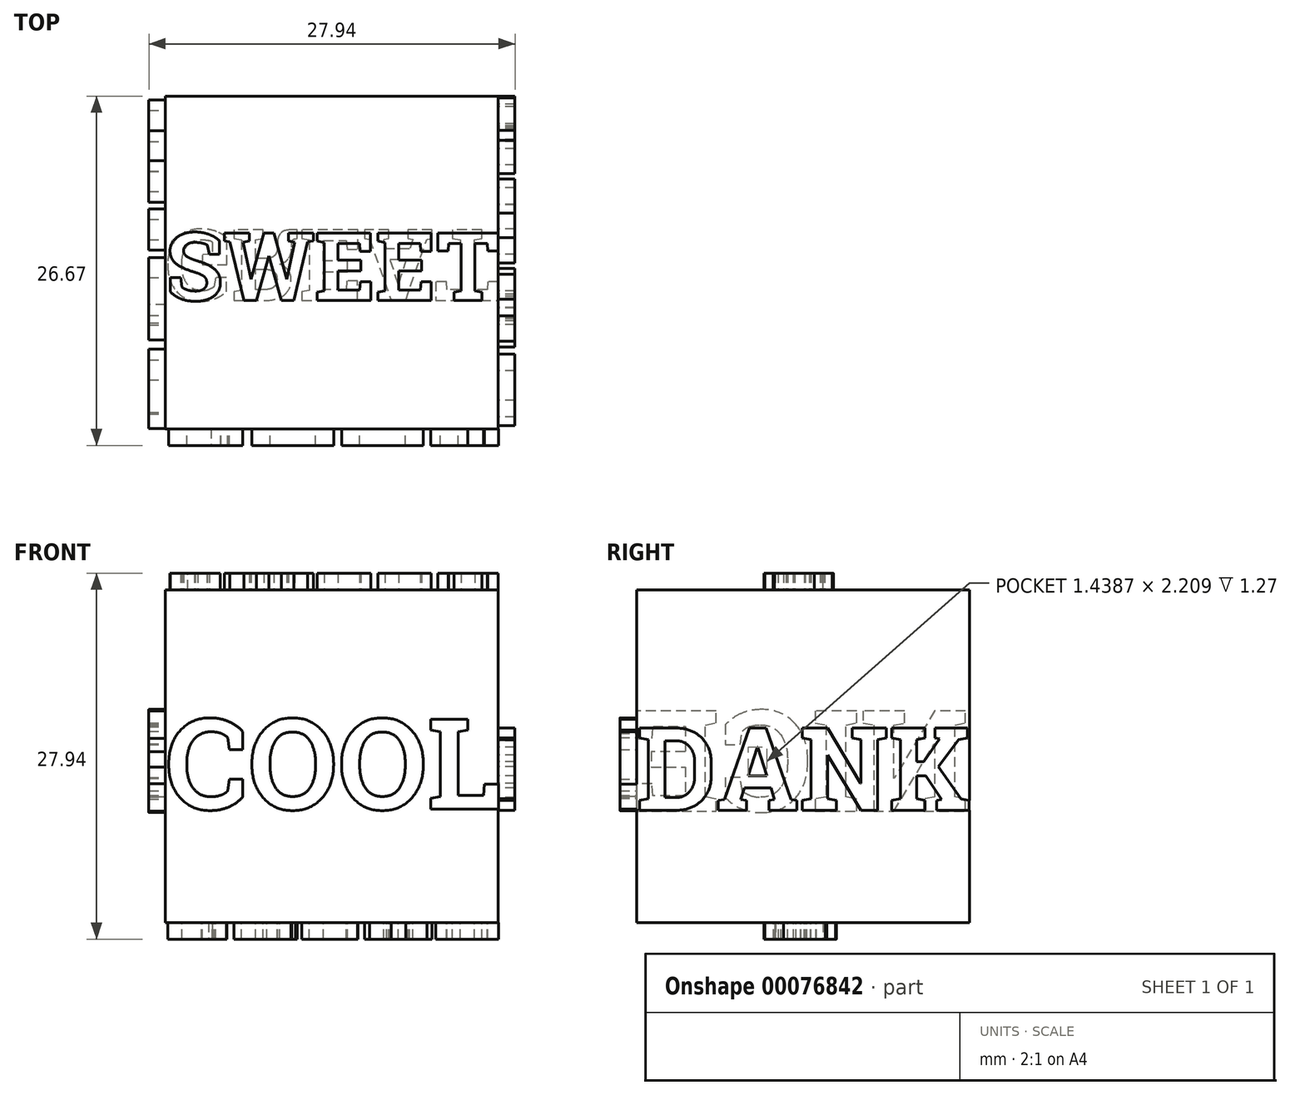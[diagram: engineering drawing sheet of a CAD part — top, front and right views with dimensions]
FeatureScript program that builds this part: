
annotation { "Feature Type Name" : "Feature", "Feature Type Description" : "" }
export const myFeature = defineFeature(function(context is Context, id is Id, definition is map)
    precondition{}
    {
        {
            var Q0;
            Q0=qCreatedBy(makeId("Front.planeOp"),FACE);
            var sketch = newSketch(context, id + "F0", { "sketchPlane" : qUnion([Q0])});
            skLineSegment(sketch, "E0.bottom", {"start": v(-11.94, 10.98) * mm, "end": v(13.46, 10.98) * mm});
            skLineSegment(sketch, "E0.top", {"start": v(-11.94, -14.42) * mm, "end": v(13.46, -14.42) * mm});
            skLineSegment(sketch, "E0.left", {"start": v(-11.94, 10.98) * mm, "end": v(-11.94, -14.42) * mm});
            skLineSegment(sketch, "E0.right", {"start": v(13.46, 10.98) * mm, "end": v(13.46, -14.42) * mm});
            skSolve(sketch);
        }
        {
            var Q0;
            Q0 = qSketchRegion(id + "F0", true);
            extrude(context, id + "F1", {"entities" : qUnion([Q0]), "depth" : 25.4 * mm});
        }
        {
            var Q0;
            Q0=makeQuery(id+"F1.opExtrude","CAP_FACE",FACE,{"disambiguationData":[OSD([sQuery(id+"F0.wireOp",EDGE,"E0.bottom"),sQuery(id+"F0.wireOp",EDGE,"E0.top"),sQuery(id+"F0.wireOp",EDGE,"E0.left"),sQuery(id+"F0.wireOp",EDGE,"E0.right")])],"isStart":false});
            var sketch = newSketch(context, id + "F2", { "sketchPlane" : qUnion([Q0])});
            skText(sketch, "E1", { "text": "COOL", "fontName": "RobotoSlab-Bold.ttf"});
            const initialGuessF2  = {"E1": [-0.01194, -0.00578, 1, 0, 0.00697]};
            skSetInitialGuess(sketch, initialGuessF2);
            skSolve(sketch);
        }
        {
            var Q0;
            Q0 = qSketchRegion(id + "F2", true);
            extrude(context, id + "F3", {"entities" : qUnion([Q0]), "operationType" : NewBodyOperationType.ADD, "depth" : 1.27 * mm});
        }
        {
            var Q0;
            Q0=makeQuery(id+"F3.boolean.opBoolean","MERGE",FACE,{"derivedFrom":[makeQuery(id+"F1.opExtrude","SWEPT_FACE",FACE,{"disambiguationData":[OSD([sQuery(id+"F0.wireOp",EDGE,"E0.right")])]}),makeQuery(id+"F3.opExtrude","SWEPT_FACE",FACE,{"disambiguationData":[OSD([sQuery(id+"F2.wireOp",EDGE,"E1.sketch_text.stroke-78")])]})]});
            var sketch = newSketch(context, id + "F4", { "sketchPlane" : qUnion([Q0])});
            skText(sketch, "E2", { "text": "DANK", "fontName": "RobotoSlab-Bold.ttf"});
            const initialGuessF4  = {"E2": [-0.0254, -0.00585, 1, 0, 0.00635]};
            skSetInitialGuess(sketch, initialGuessF4);
            skSolve(sketch);
        }
        {
            var Q0;
            Q0 = qSketchRegion(id + "F4", true);
            extrude(context, id + "F5", {"entities" : qUnion([Q0]), "operationType" : NewBodyOperationType.ADD, "depth" : 1.27 * mm});
        }
        {
            var Q0;
            Q0=makeQuery(id+"F1.opExtrude","SWEPT_FACE",FACE,{"disambiguationData":[OSD([sQuery(id+"F0.wireOp",EDGE,"E0.left")])]});
            var sketch = newSketch(context, id + "F6", { "sketchPlane" : qUnion([Q0])});
            skText(sketch, "E3", { "text": "NICE", "fontName": "RobotoSlab-Bold.ttf"});
            const initialGuessF6  = {"E3": [0, -0.00592, 1, 0, 0.00775]};
            skSetInitialGuess(sketch, initialGuessF6);
            skSolve(sketch);
        }
        {
            var Q0;
            Q0 = qSketchRegion(id + "F6", true);
            extrude(context, id + "F7", {"entities" : qUnion([Q0]), "operationType" : NewBodyOperationType.ADD, "depth" : 1.27 * mm});
        }
        {
            var Q0;
            Q0=makeQuery(id+"F1.opExtrude","SWEPT_FACE",FACE,{"disambiguationData":[OSD([sQuery(id+"F0.wireOp",EDGE,"E0.top")])]});
            var sketch = newSketch(context, id + "F8", { "sketchPlane" : qUnion([Q0])});
            skText(sketch, "E4", { "text": "GREAT", "fontName": "RobotoSlab-Bold.ttf"});
            const initialGuessF8  = {"E4": [-0.01194, 0.01022, 1, 0, 0.00545]};
            skSetInitialGuess(sketch, initialGuessF8);
            skSolve(sketch);
        }
        {
            var Q0;
            Q0 = qSketchRegion(id + "F8", true);
            extrude(context, id + "F9", {"entities" : qUnion([Q0]), "operationType" : NewBodyOperationType.ADD, "depth" : 1.27 * mm});
        }
        {
            var Q0;
            Q0=makeQuery(id+"F1.opExtrude","SWEPT_FACE",FACE,{"disambiguationData":[OSD([sQuery(id+"F0.wireOp",EDGE,"E0.bottom")])]});
            var sketch = newSketch(context, id + "F10", { "sketchPlane" : qUnion([Q0])});
            skText(sketch, "E5", { "text": "SWEET", "fontName": "RobotoSlab-Bold.ttf"});
            const initialGuessF10  = {"E5": [-0.01194, -0.0156, 1, 0, 0.00522]};
            skSetInitialGuess(sketch, initialGuessF10);
            skSolve(sketch);
        }
        {
            var Q0;
            Q0 = qSketchRegion(id + "F10", true);
            extrude(context, id + "F11", {"entities" : qUnion([Q0]), "operationType" : NewBodyOperationType.ADD, "depth" : 1.27 * mm});
        }
    });
